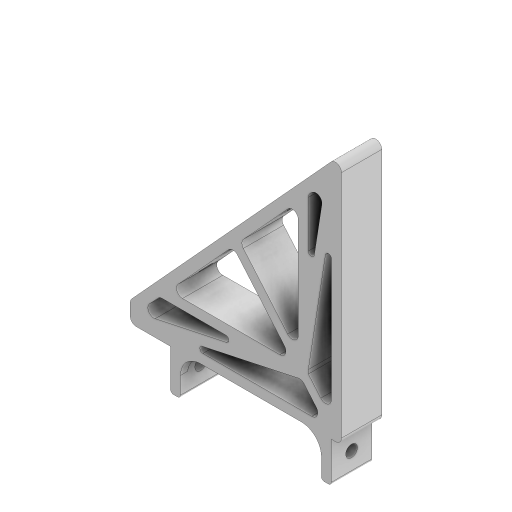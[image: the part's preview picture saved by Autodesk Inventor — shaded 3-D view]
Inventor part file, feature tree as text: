
AUTODESK INVENTOR PART (.ipt)
format: ipt  version: 2024 (Build 280153000, 153)  size: 291,328 bytes
history: native  units: mm
features: sketch x8, extrude x5, fillet x4, hole x3
ambient origin geometry x8: Origin, YZ Plane, XZ Plane, XY Plane, X Axis, Y Axis, Z Axis, Center Point
bodies: Solid1 (feature_tree)
feature tree (20):
  extrude  "Extrusion1"  Depth=10.0mm
  extrude  "Extrusion2"  Depth=5.0mm
  fillet  "Fillet1"  Radius=20.0mm
  fillet  "Fillet2"  Radius=2.5mm
  hole  "Hole1"  [1 undecoded]
  extrude  "Extrusion3"  Depth=20.0mm TaperAngle=0.0deg
  fillet  "Fillet3"  Radius=3.0mm
  fillet  "Fillet4"  Radius=5.0mm
  hole  "Hole2"  [1 undecoded]
  extrude  "Extrusion4"  Depth=1.5mm
  hole  "Hole3"  [1 undecoded]
  extrude  "Extrusion5"  Depth=10.0mm
  sketch  "Sketch1"  dims[d0=10.0mm d1=105.0mm]
  sketch  "Sketch2"  dims[d2=125.0mm d3=5.0mm d4=20.0mm d5=0.0mm d8=2.5mm]
  sketch  "Sketch4"  dims[d9=2.5mm d10=5.0mm]
  sketch  "Sketch5"  dims[d11=5.0mm d12=20.0mm d13=0.0mm d14=3.0mm d16=5.0mm]
  sketch  "Sketch6"  dims[d17=2.094395mm d18=5.0mm]
  sketch  "Sketch7"  dims[d19=1.570796mm d20=1.5mm]
  sketch  "Sketch8"  dims[d25=5.8mm d26=10.0mm d27=4.0mm d28=2.0mm d29=90.0deg d30=14.2mm d31=0.0mm d32=65.0mm]
  sketch  "Sketch9"  dims[d33=10.0mm d34=34.253mm d35=5.0mm d36=20.0mm d37=80.0mm d38=5.0mm d39=20.0mm d40=0.0mm d41=1.5mm d42=10.0mm d43=5.8mm d44=6.0mm d45=10.4mm d46=2.0mm d47=90.0deg d48=8.0mm d49=0.0mm d50=10.0mm d51=10.0mm d52=20.0mm d53=3.5mm d54=10.0mm d55=0.0mm d56=5.8mm d57=6.0mm d58=4.0mm d59=2.0mm d60=90.0deg d61=8.0mm d62=0.0mm d63=10.0mm d64=10.0mm d65=10.0mm d66=0.0mm]
note: 3 required parameter values undecoded (feature->parameter linkage not recoverable at this tier; creation-order binding heuristic only, values carry confidence <= 0.55)
